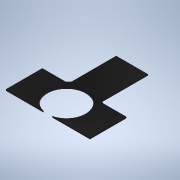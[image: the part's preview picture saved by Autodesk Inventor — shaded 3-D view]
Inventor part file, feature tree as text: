
AUTODESK INVENTOR PART (.ipt)
format: ipt  version: 2020 (Build 240168000, 168)  size: 126,464 bytes
history: native  units: in
note: dims shown in document units (in); Inventor stores cm internally (conversion verified against a paired STEP export)
features: extrude x1, sketch x1
ambient origin geometry x8: Origin, YZ Plane, XZ Plane, XY Plane, X Axis, Y Axis, Z Axis, Center Point
bodies: Solid1 (feature_tree)
feature tree (2):
  extrude  "Extrusion1"  Depth=3.8189in
  sketch  "Sketch2"  dims[d1=1.7323in d2=3.8189in d3=3.8189in d4=1.9094in d5=1.9094in d8=1.1909in d9=1.1909in d10=2.1654in d11=2.1654in d12=0.063in d13=0.0in d14=0.0in d15=45.0deg d16=0.1181in d17=0.1181in d18=0.8465in d19=1.063in]
